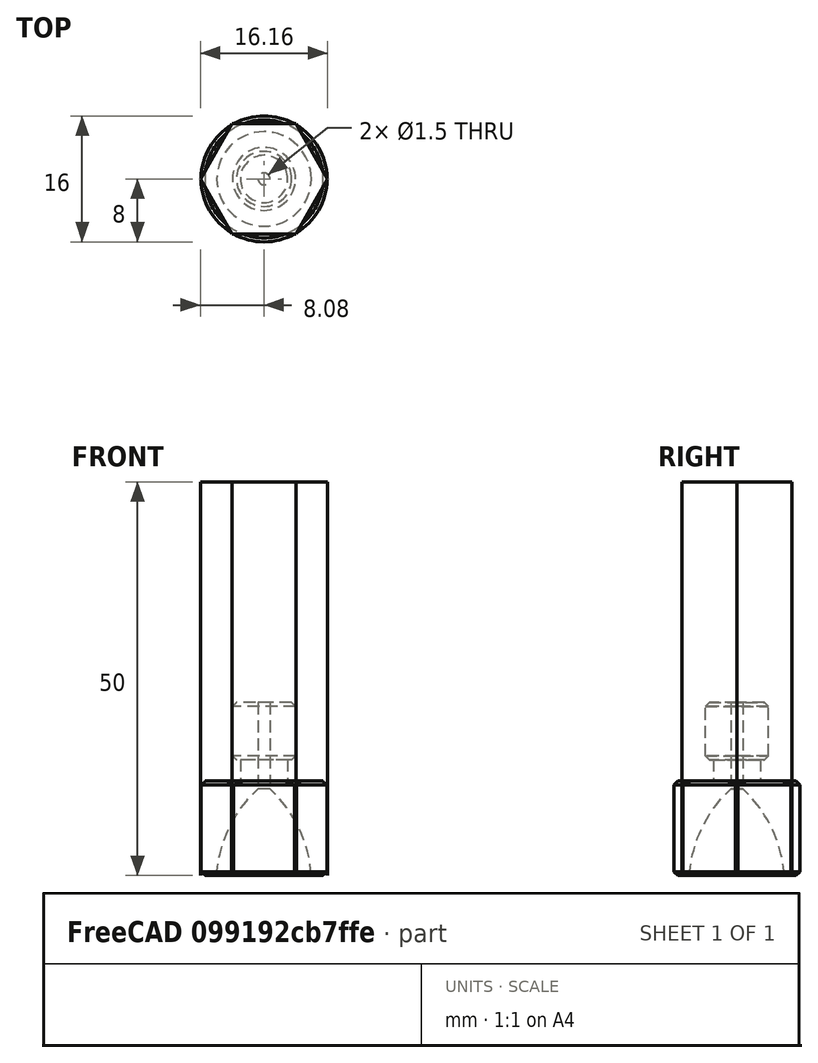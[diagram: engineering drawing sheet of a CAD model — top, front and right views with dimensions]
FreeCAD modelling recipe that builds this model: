
FCSTD DOCUMENT  (FreeCAD 0.19R24291 (Git))
Label: FilPullNozzle_v2a
License: All rights reserved
LicenseURL: http://en.wikipedia.org/wiki/All_rights_reserved
objects: TechDraw::DrawViewDimension×13, TechDraw::DrawViewBalloon×4, TechDraw::DrawViewPart×3, Sketcher::SketchObject×2, PartDesign::Body×2, PartDesign::Revolution×1, PartDesign::Pad×1, Part::MultiCommon×1, TechDraw::DrawSVGTemplate×1, TechDraw::DrawViewSection×1, TechDraw::DrawViewAnnotation×1, TechDraw::DrawPage×1
note: 9 computed .brp shape members not serialized (recipe doc carries the construction recipe); baked Part::Feature solids carry a one-line shape summary decoded from their .brp

FEATURE [Sketcher::SketchObject] Sketch
  FullyConstrained = true
  MapMode = 5
  Placement = pos=(0,0,0) rot=(1,0,0;1.5708rad)
  Support = -> [XZ_Plane]
  expr: Constraints[5] = 1.5 / 2
  sketch-geometry (13):
    g0: LineSegment StartX=0.75 StartY=22 StartZ=0 EndX=0.75 EndY=11 EndZ=0
    g1: LineSegment StartX=0.75 StartY=22 StartZ=0 EndX=3.5 EndY=22 EndZ=0
    g2: LineSegment StartX=3 StartY=12 StartZ=0 EndX=7.5 EndY=12 EndZ=0
    g3: LineSegment StartX=8 StartY=11.5 StartZ=0 EndX=8 EndY=0.5 EndZ=0
    g4: LineSegment StartX=7.5 StartY=0 StartZ=0 EndX=6 EndY=0 EndZ=0
    g5: LineSegment StartX=4 StartY=15.2 StartZ=0 EndX=4 EndY=21.5 EndZ=0
    g6: ArcOfCircle CenterX=-10.244 CenterY=-1 CenterZ=0 NormalX=0 NormalY=0 NormalZ=1 AngleXU=0 Radius=16.2748 StartAngle=0.0614834 EndAngle=0.829119
    g7: LineSegment StartX=3 StartY=14.7 StartZ=0 EndX=3 EndY=12 EndZ=0
    g8: LineSegment StartX=3 StartY=14.7 StartZ=0 EndX=3.5 EndY=14.7 EndZ=0
    g9: LineSegment StartX=3.5 StartY=22 StartZ=0 EndX=4 EndY=21.5 EndZ=0
    g10: LineSegment StartX=3.5 StartY=14.7 StartZ=0 EndX=4 EndY=15.2 EndZ=0
    g11: LineSegment StartX=7.5 StartY=12 StartZ=0 EndX=8 EndY=11.5 EndZ=0
    g12: LineSegment StartX=7.5 StartY=0 StartZ=0 EndX=8 EndY=0.5 EndZ=0
  constraints (40):
    c: Vertical(g0)
    c: PointOnObject(g4,g-1)
    c: Horizontal(g1)
    c: Horizontal(g2)
    c: Vertical(g3)
    c: DistanceX(g-2,g0) = 0.75
    c: Vertical(g5)
    c: Coincident(g6,g0)
    c: Coincident(g6,g4)
    c: DistanceY(g-1,g0) = 11
    c: Vertical(g7)
    c: Coincident(g2,g7)
    c: Coincident(g0,g1)
    c: Coincident(g8,g7)
    c: Horizontal(g8)
    c: DistanceY(g7,g7) = 2.7
    c: DistanceY(g6,g-1) = 1
    c: DistanceY(g-1,g0) = 22
    c: DistanceX(g-2,g4) = 6
    c: Coincident(g9,g1)
    c: Coincident(g9,g5)
    c: Angle(g1,g9) = 2.35619
    c: DistanceX(g-2,g5) = 4
    c: Coincident(g10,g8)
    c: Coincident(g10,g5)
    c: Distance(g5,g8) = 0.5
    c: Angle(g10,g8) = 2.35619
    c: Coincident(g11,g2)
    c: Coincident(g11,g3)
    c: Distance(g3,g2) = 0.5
    c: Angle(g2,g11) = 2.35619
    c: DistanceY(g-1,g2) = 12
    c: Distance(g5,g7) = 1
    c: Coincident(g12,g4)
    c: Coincident(g12,g3)
    c: Distance(g3,g4) = 0.5
    c: Horizontal(g4)
    c: Angle(g12,g-1) = 2.35619
    c: DistanceX(g-2,g3) = 8
    c: Distance(g5,g1) = 0.5
FEATURE [PartDesign::Revolution] Revolution
  Angle = 360
  Axis = (0,-2e-16,1)
  Base = (0,0,0)
  Placement = pos=(0,0,0) rot=(1,0,0;1.5708rad)
  Profile = -> Sketch
  ReferenceAxis = -> Sketch [V_Axis]
  Reversed = true
FEATURE [PartDesign::Body] Body
  Group = -> [Sketch,Revolution]
  Origin = -> Origin
  Tip = -> Revolution
FEATURE [Sketcher::SketchObject] Sketch001
  FullyConstrained = true
  MapMode = 5
  Support = -> [XY_Plane001]
  sketch-geometry (7):
    g0: LineSegment StartX=8.0829 StartY=0 StartZ=0 EndX=4.04145 EndY=7 EndZ=0
    g1: LineSegment StartX=4.04145 StartY=7 StartZ=0 EndX=-4.04145 EndY=7 EndZ=0
    g2: LineSegment StartX=-4.04145 StartY=7 StartZ=0 EndX=-8.0829 EndY=-1.8e-15 EndZ=0
    g3: LineSegment StartX=-8.0829 StartY=-1.8e-15 StartZ=0 EndX=-4.04145 EndY=-7 EndZ=0
    g4: LineSegment StartX=-4.04145 StartY=-7 StartZ=0 EndX=4.04145 EndY=-7 EndZ=0
    g5: LineSegment StartX=4.04145 StartY=-7 StartZ=0 EndX=8.0829 EndY=0 EndZ=0
    g6: Circle CenterX=0 CenterY=0 CenterZ=0 NormalX=0 NormalY=0 NormalZ=1 AngleXU=0 Radius=8.0829
  constraints (16):
    c: Coincident(g0,g1)
    c: Coincident(g1,g2)
    c: Coincident(g2,g3)
    c: Coincident(g3,g4)
    c: Coincident(g4,g5)
    c: Coincident(g5,g0)
    c: Equal(g0, g1-g5) x5
    c: PointOnObject(g0,g6)
    c: PointOnObject(g1,g6)
    c: PointOnObject(g2,g6)
    c: PointOnObject(g3,g6)
    c: PointOnObject(g4,g6)
    c: PointOnObject(g5,g6)
    c: Coincident(g6,g-1)
    c: PointOnObject(g5,g-1)
    c: Distance(g0,g3) = 14
FEATURE [PartDesign::Pad] Pad
  Direction = (1,1,1)
  Length = 50
  Length2 = 100
  Profile = -> Sketch001
  Type = 0
FEATURE [PartDesign::Body] Body001
  Group = -> [Sketch001,Pad]
  Origin = -> Origin001
  Tip = -> Pad
FEATURE [Part::MultiCommon] Common
  Shapes = -> [Revolution,Pad]
FEATURE [TechDraw::DrawSVGTemplate] Template
  Height = 210
  Orientation = 1
  Width = 297
FEATURE [TechDraw::DrawViewPart] View
  CoarseView = false
  Direction = (0.577,-0.577,0.577)
  Focus = 100
  HardHidden = false
  IsoCount = 0
  IsoHidden = false
  IsoVisible = false
  LockPosition = false
  Perspective = false
  Rotation = 0
  Scale = 3
  ScaleType = 0
  SeamHidden = false
  SeamVisible = true
  SmoothHidden = false
  SmoothVisible = true
  Source = -> [Common]
  X = 258.184
  XDirection = (0.707,0.707,0)
  Y = 154.873
FEATURE [TechDraw::DrawViewPart] View001
  CoarseView = false
  Direction = (0,-1,0)
  Focus = 100
  HardHidden = false
  IsoCount = 0
  IsoHidden = false
  IsoVisible = false
  LockPosition = false
  Perspective = false
  Rotation = 0
  Scale = 3
  ScaleType = 0
  SeamHidden = false
  SeamVisible = true
  SmoothHidden = false
  SmoothVisible = true
  Source = -> [Common]
  X = 52.0975
  XDirection = (1,0,0)
  Y = 148.503
FEATURE [TechDraw::DrawViewSection] SectionView  label="Section A - A"
  BaseView = -> View001
  Caption = A-A
  CoarseView = false
  CutSurfaceDisplay = 2
  Direction = (1,0,0)
  FileGeomPattern = <path>
  FileHatchPattern = <path>
  Focus = 100
  FuseBeforeCut = false
  HardHidden = false
  HatchScale = 1
  IsoCount = 0
  IsoHidden = false
  IsoVisible = false
  LockPosition = false
  NameGeomPattern = Diamond
  Perspective = false
  Rotation = 0
  Scale = 5
  ScaleType = 0
  SeamHidden = false
  SeamVisible = true
  SectionDirection = 1
  SectionNormal = (1,0,0)
  SectionOrigin = (0,0,10.9)
  SectionSymbol = A
  SmoothHidden = false
  SmoothVisible = true
  Source = -> [Common]
  X = 155.713
  XDirection = (0,1,0)
  Y = 111.714
FEATURE [TechDraw::DrawViewDimension] Dimension
  Arbitrary = false
  ArbitraryTolerances = false
  EqualTolerance = true
  FormatSpec = %.2f
  FormatSpecOverTolerance = %+.2f
  FormatSpecUnderTolerance = %+.2f
  Inverted = false
  LockPosition = false
  MeasureType = 1
  OverTolerance = 0
  References2D = -> [SectionView]
  Rotation = 0
  ScaleType = 0
  TheoreticalExact = false
  Type = 0
  UnderTolerance = 0
  X = -51.8318
  Y = 26.629
FEATURE [TechDraw::DrawViewDimension] Dimension005
  Arbitrary = false
  ArbitraryTolerances = false
  EqualTolerance = true
  FormatSpec = %.2f
  FormatSpecOverTolerance = %+.2f
  FormatSpecUnderTolerance = %+.2f
  Inverted = false
  LockPosition = false
  MeasureType = 1
  OverTolerance = 0
  References2D = -> [SectionView]
  Rotation = 0
  ScaleType = 0
  TheoreticalExact = false
  Type = 0
  UnderTolerance = 0
  X = 11.6931
  Y = 74.1729
FEATURE [TechDraw::DrawViewPart] View002
  CoarseView = false
  Direction = (0,0,-1)
  Focus = 100
  HardHidden = false
  IsoCount = 0
  IsoHidden = false
  IsoVisible = false
  LockPosition = false
  Perspective = false
  Rotation = 0
  Scale = 3
  ScaleType = 0
  SeamHidden = false
  SeamVisible = true
  SmoothHidden = false
  SmoothVisible = true
  Source = -> [Common]
  X = 53.5076
  XDirection = (1,0,0)
  Y = 49.0847
FEATURE [TechDraw::DrawViewDimension] Dimension008
  Arbitrary = false
  ArbitraryTolerances = false
  EqualTolerance = true
  FormatSpec = %.2f
  FormatSpecOverTolerance = %+.2f
  FormatSpecUnderTolerance = %+.2f
  Inverted = false
  LockPosition = false
  MeasureType = 1
  OverTolerance = 0
  References2D = -> [View002]
  Rotation = 0
  ScaleType = 0
  TheoreticalExact = false
  Type = 0
  UnderTolerance = 0
  X = -17.0297
  Y = 28.5888
FEATURE [TechDraw::DrawViewDimension] Dimension009
  Arbitrary = false
  ArbitraryTolerances = false
  EqualTolerance = true
  FormatSpec = %.2f
  FormatSpecOverTolerance = %+.2f
  FormatSpecUnderTolerance = %+.2f
  Inverted = false
  LockPosition = false
  MeasureType = 1
  OverTolerance = 0
  References2D = -> [SectionView]
  Rotation = 0
  ScaleType = 0
  TheoreticalExact = false
  Type = 0
  UnderTolerance = 0
  X = 68.8891
  Y = -7.96581
FEATURE [TechDraw::DrawViewDimension] Dimension010
  Arbitrary = false
  ArbitraryTolerances = false
  EqualTolerance = true
  FormatSpec = %.2f
  FormatSpecOverTolerance = %+.2f
  FormatSpecUnderTolerance = %+.2f
  Inverted = false
  LockPosition = false
  MeasureType = 1
  OverTolerance = 0
  References2D = -> [SectionView]
  Rotation = 0
  ScaleType = 0
  TheoreticalExact = false
  Type = 0
  UnderTolerance = 0
  X = 42.8719
  Y = 29.44
FEATURE [TechDraw::DrawViewDimension] Dimension011
  Arbitrary = false
  ArbitraryTolerances = false
  EqualTolerance = true
  FormatSpec = %.2f
  FormatSpecOverTolerance = %+.2f
  FormatSpecUnderTolerance = %+.2f
  Inverted = false
  LockPosition = false
  MeasureType = 1
  OverTolerance = 0
  References2D = -> [SectionView]
  Rotation = 0
  ScaleType = 0
  TheoreticalExact = false
  Type = 0
  UnderTolerance = 0
  X = -43.0219
  Y = 15.8738
FEATURE [TechDraw::DrawViewDimension] Dimension012
  Arbitrary = false
  ArbitraryTolerances = false
  EqualTolerance = true
  FormatSpec = %.2f
  FormatSpecOverTolerance = %+.2f
  FormatSpecUnderTolerance = %+.2f
  Inverted = false
  LockPosition = false
  MeasureType = 1
  OverTolerance = 0
  References2D = -> [SectionView]
  Rotation = 0
  ScaleType = 0
  TheoreticalExact = false
  Type = 0
  UnderTolerance = 0
  X = -42.0953
  Y = 37.9653
FEATURE [TechDraw::DrawViewDimension] Dimension013
  Arbitrary = false
  ArbitraryTolerances = false
  EqualTolerance = true
  FormatSpec = %.2f
  FormatSpecOverTolerance = %+.2f
  FormatSpecUnderTolerance = %+.2f
  Inverted = false
  LockPosition = false
  MeasureType = 1
  OverTolerance = 0
  References2D = -> [SectionView]
  Rotation = 0
  ScaleType = 0
  TheoreticalExact = false
  Type = 0
  UnderTolerance = 0
  X = 49.098
  Y = -29.0008
FEATURE [TechDraw::DrawViewDimension] Dimension014
  Arbitrary = false
  ArbitraryTolerances = false
  EqualTolerance = true
  FormatSpec = %.2f
  FormatSpecOverTolerance = %+.2f
  FormatSpecUnderTolerance = %+.2f
  Inverted = false
  LockPosition = false
  MeasureType = 1
  OverTolerance = 0
  References2D = -> [View002]
  Rotation = 0
  ScaleType = 0
  TheoreticalExact = false
  Type = 0
  UnderTolerance = 0
  X = -0.153464
  Y = -26.3818
FEATURE [TechDraw::DrawViewBalloon] Balloon
  BubbleShape = 0
  EndType = 0
  EndTypeScale = 1
  KinkLength = 5
  LockPosition = false
  OriginX = 3.90201
  OriginY = 7.22494
  Rotation = 0
  ScaleType = 0
  ShapeScale = 1
  SourceView = -> View001
  Text = 1
  TextWrapLen = -1
  X = 10.5687
  Y = 13.8916
FEATURE [TechDraw::DrawViewDimension] Dimension015
  Arbitrary = false
  ArbitraryTolerances = false
  EqualTolerance = true
  FormatSpec = %.2f
  FormatSpecOverTolerance = %+.2f
  FormatSpecUnderTolerance = %+.2f
  Inverted = false
  LockPosition = false
  MeasureType = 1
  OverTolerance = 0
  References2D = -> [SectionView]
  Rotation = 0
  ScaleType = 0
  TheoreticalExact = false
  Type = 2
  UnderTolerance = 0
  X = 49.0617
  Y = 30
FEATURE [TechDraw::DrawViewDimension] Dimension016
  Arbitrary = false
  ArbitraryTolerances = false
  EqualTolerance = true
  FormatSpec = %.2f
  FormatSpecOverTolerance = %+.2f
  FormatSpecUnderTolerance = %+.2f
  Inverted = false
  LockPosition = false
  MeasureType = 1
  OverTolerance = 0
  References2D = -> [SectionView]
  Rotation = 0
  ScaleType = 0
  TheoreticalExact = false
  Type = 0
  UnderTolerance = 0
  X = 1.4501
  Y = -20.4877
FEATURE [TechDraw::DrawViewDimension] Dimension017
  Arbitrary = false
  ArbitraryTolerances = false
  EqualTolerance = true
  FormatSpec = %.2f
  FormatSpecOverTolerance = %+.2f
  FormatSpecUnderTolerance = %+.2f
  Inverted = false
  LockPosition = false
  MeasureType = 1
  OverTolerance = 0
  References2D = -> [SectionView]
  Rotation = 0
  ScaleType = 0
  TheoreticalExact = false
  Type = 0
  UnderTolerance = 0
  X = 13.8697
  Y = 65.6063
FEATURE [TechDraw::DrawViewBalloon] Balloon001
  BubbleShape = 0
  EndType = 0
  EndTypeScale = 1
  KinkLength = 5
  LockPosition = false
  OriginX = 0.0128292
  OriginY = 8.67374
  Rotation = 0
  ScaleType = 0
  ShapeScale = 1
  SourceView = -> SectionView
  Text = 2
  TextWrapLen = -1
  X = 8.76816
  Y = 12.8136
FEATURE [TechDraw::DrawViewAnnotation] Annotation
  Font = osifont
  LineSpace = 80
  LockPosition = false
  MaxWidth = -1
  Rotation = 0
  ScaleType = 0
  Text = 1. Thread M8 | 2. Channel need to be extended by reamer to 1.7-1.8 mm | 3. Made by "arrow head" drill bit for ceramics 12 mm size
  TextSize = 5
  TextStyle = 0
  X = 157.5
  Y = 36
FEATURE [TechDraw::DrawViewDimension] Dimension018
  Arbitrary = false
  ArbitraryTolerances = false
  EqualTolerance = true
  FormatSpec = %.2f
  FormatSpecOverTolerance = %+.2f
  FormatSpecUnderTolerance = %+.2f
  Inverted = false
  LockPosition = false
  MeasureType = 1
  OverTolerance = 0
  References2D = -> [SectionView]
  Rotation = 0
  ScaleType = 0
  TheoreticalExact = false
  Type = 0
  UnderTolerance = 0
  X = -58.7122
  Y = -29.4062
FEATURE [TechDraw::DrawViewBalloon] Balloon002
  BubbleShape = 0
  EndType = 0
  EndTypeScale = 1
  KinkLength = 5
  LockPosition = false
  OriginX = -4.20168
  OriginY = 8.41066
  Rotation = 0
  ScaleType = 0
  ShapeScale = 1
  SourceView = -> SectionView
  Text = 1
  TextWrapLen = -1
  X = -10.1775
  Y = 15.5877
FEATURE [TechDraw::DrawViewBalloon] Balloon003
  BubbleShape = 0
  EndType = 0
  EndTypeScale = 1
  KinkLength = 5
  LockPosition = false
  OriginX = -3.88398
  OriginY = -3.59842
  Rotation = 0
  ScaleType = 0
  ShapeScale = 1
  SourceView = -> SectionView
  Text = 3
  TextWrapLen = -1
  X = -13.6086
  Y = -2.20357
FEATURE [TechDraw::DrawPage] Page
  KeepUpdated = true
  NextBalloonIndex = 7
  ProjectionType = 0
  Template = -> Template
  Views = -> [View,View001,SectionView,Dimension,Dimension005,View002,Dimension008,Dimension009,Dimension010,Dimension011,Dimension012,Dimension013,Dimension014,Balloon,Dimension015,Dimension016,Dimension017,Balloon001,Annotation,Dimension018,Balloon002,Balloon003]
note: 2 file-system paths scrubbed to <path> (originals preserved in the JSON sidecar)
